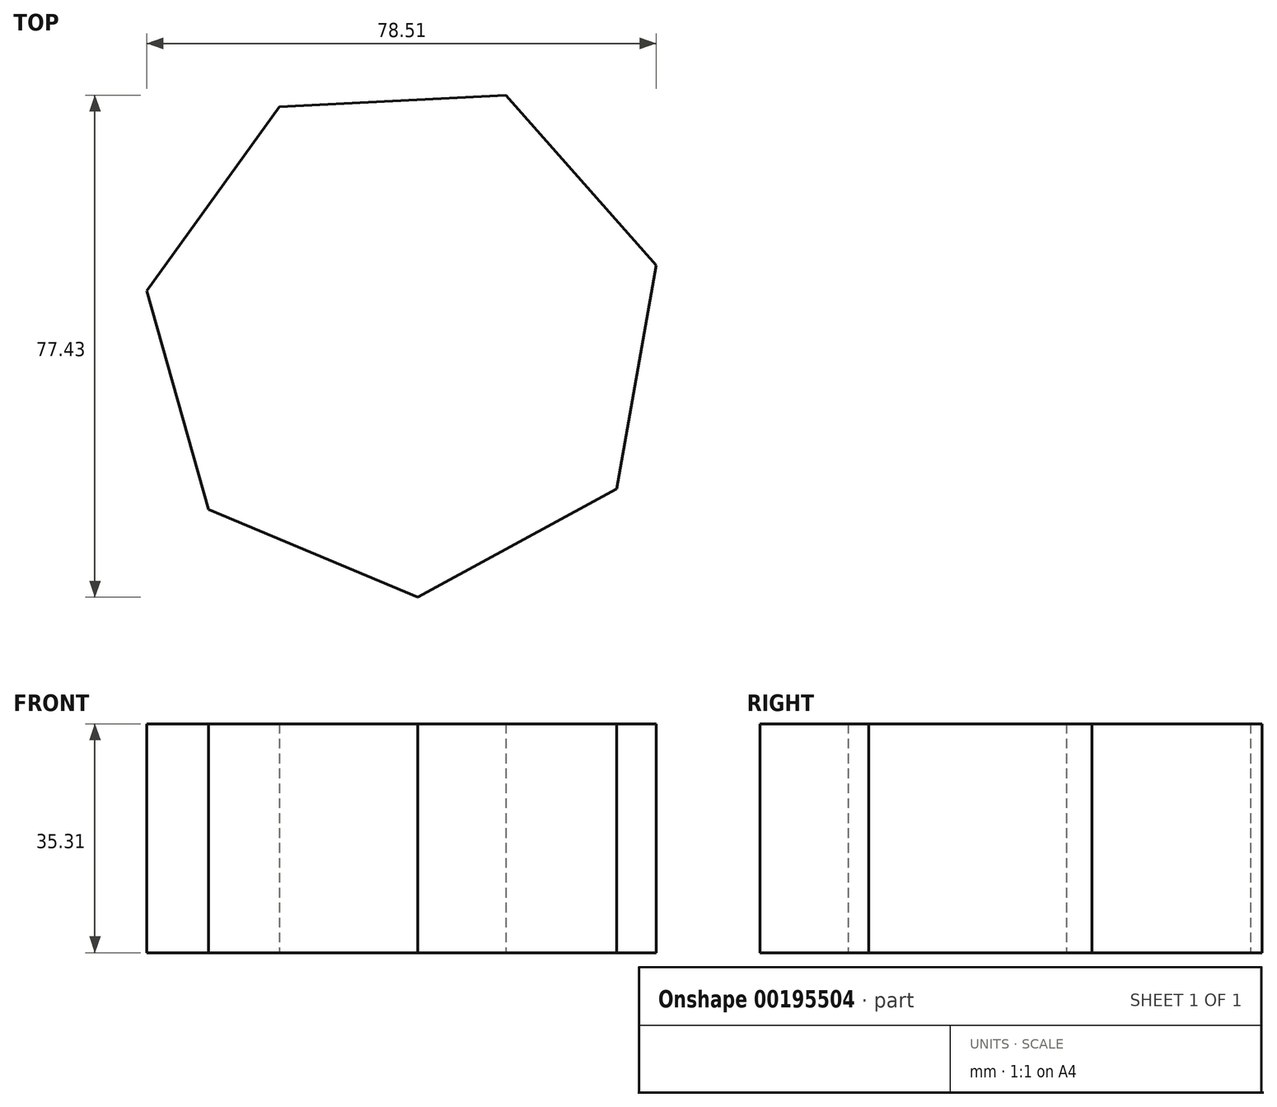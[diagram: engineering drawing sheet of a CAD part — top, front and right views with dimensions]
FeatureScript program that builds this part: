
annotation { "Feature Type Name" : "Feature", "Feature Type Description" : "" }
export const myFeature = defineFeature(function(context is Context, id is Id, definition is map)
    precondition{}
    {
        {
            var Q0;
            Q0=qCreatedBy(makeId("Top.planeOp"),FACE);
            var sketch = newSketch(context, id + "F0", { "sketchPlane" : qUnion([Q0])});
            skCircle(sketch, "E0.cCircle", {"center": v(0, -10.71) * mm, "radius": 36.32 * mm, "construction": true});
            skLineSegment(sketch, "E0.0", {"start": v(2.03, -50.98) * mm, "end": v(-30.21, -37.4) * mm});
            skLineSegment(sketch, "E0.1", {"start": v(-30.21, -37.4) * mm, "end": v(-39.7, -3.73) * mm});
            skLineSegment(sketch, "E0.2", {"start": v(-39.7, -3.73) * mm, "end": v(-19.3, 24.68) * mm});
            skLineSegment(sketch, "E0.3", {"start": v(-19.3, 24.68) * mm, "end": v(15.64, 26.45) * mm});
            skLineSegment(sketch, "E0.4", {"start": v(15.64, 26.45) * mm, "end": v(38.8, 0.23) * mm});
            skLineSegment(sketch, "E0.5", {"start": v(38.8, 0.23) * mm, "end": v(32.75, -34.23) * mm});
            skLineSegment(sketch, "E0.6", {"start": v(32.75, -34.23) * mm, "end": v(2.03, -50.98) * mm});
            skPoint(sketch, "E0.0.midPoint", {"position": v(-14.1, -44.2) * mm});
            skSolve(sketch);
        }
        {
            var Q0;
            Q0=makeQuery(id+"F0.imprint","IMPRINT",FACE,{"disambiguationData":[TD([[makeQuery(id+"F0.imprint","IMPRINT",EDGE,{"derivedFrom":sQuery(id+"F0.wireOp",EDGE,"E0.0")}),-1.0]])]});
            extrude(context, id + "F1", {"entities" : qUnion([Q0]), "depth" : 35.3 * mm});
        }
    });
